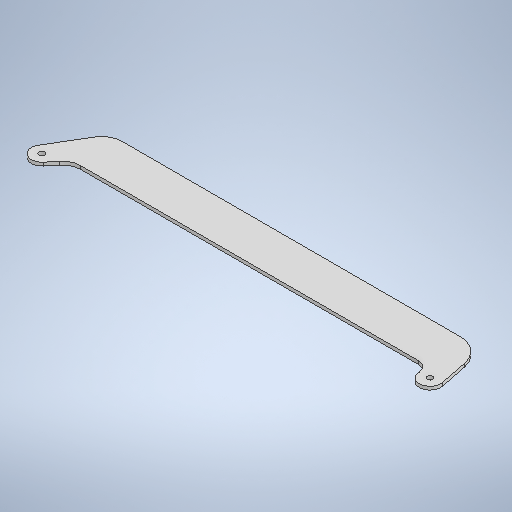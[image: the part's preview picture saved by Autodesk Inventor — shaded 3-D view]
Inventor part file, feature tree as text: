
AUTODESK INVENTOR PART (.ipt)
format: ipt  version: 2025.2 (Build 292293000, 293)  size: 281,600 bytes
history: native  units: in
note: dims shown in document units (in); Inventor stores cm internally (conversion verified against a paired STEP export)
features: extrude x2, sketch x2
ambient origin geometry x8: Origin, YZ Plane, XZ Plane, XY Plane, X Axis, Y Axis, Z Axis, Center Point
bodies: Solid1 (feature_tree)
feature tree (4):
  extrude  "Extrusion1"  Depth=0.4291in
  extrude  "Extrusion2"  TaperAngle=0.0deg  [1 undecoded]
  sketch  "Sketch1"  dims[d0=0.4291in d1=0.4291in]
  sketch  "Sketch2"  dims[d2=7.874in d3=0.0in d6=0.0in d7=0.0in d8=0.0in d9=6.8568in d10=0.3664in d11=0.5179in d12=0.0669in d13=0.0in d14=0.1181in d15=0.1181in d16=0.0669in d17=0.0in]
note: 1 required parameter value undecoded (feature->parameter linkage not recoverable at this tier; creation-order binding heuristic only, values carry confidence <= 0.55)
